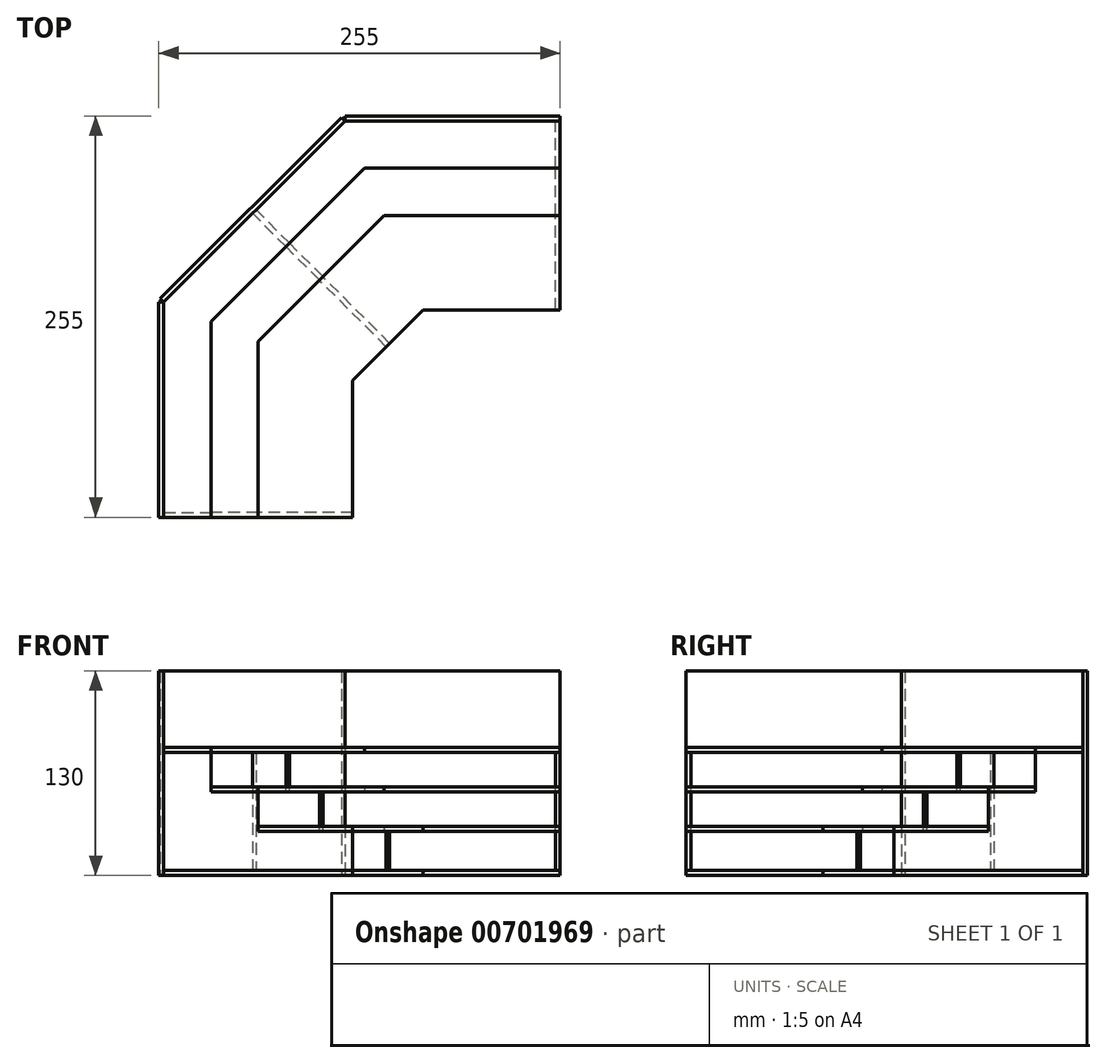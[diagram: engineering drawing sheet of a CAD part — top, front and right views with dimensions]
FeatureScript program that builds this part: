
annotation { "Feature Type Name" : "Feature", "Feature Type Description" : "" }
export const myFeature = defineFeature(function(context is Context, id is Id, definition is map)
    precondition{}
    {
        {
            assignVariable(context, id + "F0", {"name" : "x", "anyValue" : 3.15});
        }
        {
            var Q0;
            Q0=qCreatedBy(makeId("Top.planeOp"),FACE);
            var sketch = newSketch(context, id + "F1", { "sketchPlane" : qUnion([Q0])});
            skLineSegment(sketch, "E0", {"start": v(0, 0) * mm, "end": v(120, 0) * mm});
            skLineSegment(sketch, "E1", {"start": v(120, 0) * mm, "end": v(120, 87) * mm});
            skLineSegment(sketch, "E2", {"start": v(120, 87) * mm, "end": v(164.85, 131.85) * mm});
            skLineSegment(sketch, "E3", {"start": v(164.85, 131.85) * mm, "end": v(251.85, 131.85) * mm});
            skLineSegment(sketch, "E4", {"start": v(251.85, 131.85) * mm, "end": v(251.85, 251.85) * mm});
            skLineSegment(sketch, "E5", {"start": v(251.85, 251.85) * mm, "end": v(115.14, 251.85) * mm});
            skLineSegment(sketch, "E6", {"start": v(115.14, 251.85) * mm, "end": v(0, 136.7) * mm});
            skLineSegment(sketch, "E7", {"start": v(0, 136.7) * mm, "end": v(0, 0) * mm});
            skLineSegment(sketch, "E8", {"start": v(0, 136.7) * mm, "end": v(0, 251.85) * mm, "construction": true});
            skLineSegment(sketch, "E9", {"start": v(0, 251.85) * mm, "end": v(115.14, 251.85) * mm, "construction": true});
            skLineSegment(sketch, "E10", {"start": v(251.85, 131.85) * mm, "end": v(251.85, 0) * mm, "construction": true});
            skLineSegment(sketch, "E11", {"start": v(251.85, 0) * mm, "end": v(120, 0) * mm, "construction": true});
            skLineSegment(sketch, "E12", {"start": v(251.85, 0) * mm, "end": v(142.42, 109.42) * mm, "construction": true});
            skLineSegment(sketch, "E13", {"start": v(142.43, 109.42) * mm, "end": v(57.57, 194.28) * mm, "construction": true});
            skLineSegment(sketch, "E14", {"start": v(57.57, 194.28) * mm, "end": v(0, 251.85) * mm, "construction": true});
            skLineSegment(sketch, "E15.0", {"start": v(-3.15, 104.14) * mm, "end": v(-3.15, 0) * mm});
            skSolve(sketch);
        }
        {
            var Q0;
            Q0=qSketchRegion(id+"F1",true);
            extrude(context, id + "F2", {"entities" : qUnion([Q0]), "depth" : (getVariable(context, 'x')) * mm, "offsetDistance" : 25 * mm});
        }
        {
            var Q0;
            Q0=makeQuery(id+"F2.opExtrude","SWEPT_FACE",FACE,{"disambiguationData":[OSD([sQuery(id+"F1.wireOp",EDGE,"E0")])]});
            var sketch = newSketch(context, id + "F3", { "sketchPlane" : qUnion([Q0])});
            skLineSegment(sketch, "E16.bottom", {"start": v(0, 3.15) * mm, "end": v(120, 3.15) * mm});
            skLineSegment(sketch, "E16.top", {"start": v(0, 78.15) * mm, "end": v(30, 78.15) * mm});
            skLineSegment(sketch, "E16.left", {"start": v(0, 3.15) * mm, "end": v(0, 78.15) * mm});
            skLineSegment(sketch, "E16.right", {"start": v(120, 3.15) * mm, "end": v(120, 28.15) * mm});
            skLineSegment(sketch, "E17", {"start": v(120, 28.15) * mm, "end": v(60, 28.15) * mm});
            skLineSegment(sketch, "E18", {"start": v(60, 28.15) * mm, "end": v(60, 53.15) * mm});
            skLineSegment(sketch, "E19", {"start": v(60, 53.15) * mm, "end": v(30, 53.15) * mm});
            skLineSegment(sketch, "E20", {"start": v(30, 53.15) * mm, "end": v(30, 78.15) * mm});
            skSolve(sketch);
        }
        {
            var Q0;
            Q0=qSketchRegion(id+"F3",true);
            extrude(context, id + "F4", {"entities" : qUnion([Q0]), "oppositeDirection" : true, "depth" : (getVariable(context, 'x')) * mm, "offsetDistance" : 25 * mm});
        }
        {
            var Q0;
            Q0=makeQuery(id+"F2.opExtrude","SWEPT_FACE",FACE,{"disambiguationData":[OSD([sQuery(id+"F1.wireOp",EDGE,"E4")])]});
            var sketch = newSketch(context, id + "F5", { "sketchPlane" : qUnion([Q0])});
            skLineSegment(sketch, "E21.bottom", {"start": v(221.85, 78.15) * mm, "end": v(251.85, 78.15) * mm});
            skLineSegment(sketch, "E21.top", {"start": v(131.85, 3.15) * mm, "end": v(251.85, 3.15) * mm});
            skLineSegment(sketch, "E21.left", {"start": v(131.85, 28.15) * mm, "end": v(131.85, 3.15) * mm});
            skLineSegment(sketch, "E21.right", {"start": v(251.85, 78.15) * mm, "end": v(251.85, 3.15) * mm});
            skLineSegment(sketch, "E22", {"start": v(131.85, 28.15) * mm, "end": v(191.85, 28.15) * mm});
            skLineSegment(sketch, "E23", {"start": v(191.85, 28.15) * mm, "end": v(191.85, 53.15) * mm});
            skLineSegment(sketch, "E24", {"start": v(191.85, 53.15) * mm, "end": v(221.85, 53.15) * mm});
            skLineSegment(sketch, "E25", {"start": v(221.85, 53.15) * mm, "end": v(221.85, 78.15) * mm});
            skSolve(sketch);
        }
        {
            var Q0;
            Q0=qSketchRegion(id+"F5",true);
            extrude(context, id + "F6", {"entities" : qUnion([Q0]), "oppositeDirection" : true, "depth" : (getVariable(context, 'x')) * mm, "offsetDistance" : 25 * mm});
        }
        {
            var Q0;
            Q0=makeQuery(id+"F2.opExtrude","SWEPT_FACE",FACE,{"disambiguationData":[OSD([sQuery(id+"F1.wireOp",EDGE,"E7")])]});
            var sketch = newSketch(context, id + "F7", { "sketchPlane" : qUnion([Q0])});
            skLineSegment(sketch, "E26.bottom", {"start": v(0, 0) * mm, "end": v(-136.7, 0) * mm});
            skLineSegment(sketch, "E26.top", {"start": v(0, 130) * mm, "end": v(-136.7, 130) * mm});
            skLineSegment(sketch, "E26.left", {"start": v(0, 130) * mm, "end": v(0, 0) * mm});
            skLineSegment(sketch, "E26.right", {"start": v(-136.7, 130) * mm, "end": v(-136.7, 0) * mm});
            skSolve(sketch);
        }
        {
            var Q0;
            Q0=qSketchRegion(id+"F7",true);
            extrude(context, id + "F8", {"entities" : qUnion([Q0]), "depth" : (getVariable(context, 'x')) * mm, "offsetDistance" : 25 * mm});
        }
        {
            var Q0;
            Q0=makeQuery(id+"F2.opExtrude","SWEPT_FACE",FACE,{"disambiguationData":[OSD([sQuery(id+"F1.wireOp",EDGE,"E5")])]});
            var sketch = newSketch(context, id + "F9", { "sketchPlane" : qUnion([Q0])});
            skLineSegment(sketch, "E27.bottom", {"start": v(-251.85, 0) * mm, "end": v(-115.14, 0) * mm});
            skLineSegment(sketch, "E27.top", {"start": v(-251.85, 130) * mm, "end": v(-115.14, 130) * mm});
            skLineSegment(sketch, "E27.left", {"start": v(-251.85, 130) * mm, "end": v(-251.85, 0) * mm});
            skLineSegment(sketch, "E27.right", {"start": v(-115.14, 130) * mm, "end": v(-115.14, 0) * mm});
            skSolve(sketch);
        }
        {
            var Q0;
            Q0=qSketchRegion(id+"F9",true);
            extrude(context, id + "F10", {"entities" : qUnion([Q0]), "depth" : (getVariable(context, 'x')) * mm, "offsetDistance" : 25 * mm});
        }
        {
            var Q0;
            Q0=makeQuery(id+"F2.opExtrude","SWEPT_FACE",FACE,{"disambiguationData":[OSD([sQuery(id+"F1.wireOp",EDGE,"E6")])]});
            var sketch = newSketch(context, id + "F11", { "sketchPlane" : qUnion([Q0])});
            skLineSegment(sketch, "E28.bottom", {"start": v(-259.5, 0) * mm, "end": v(-96.67, 0) * mm});
            skLineSegment(sketch, "E28.top", {"start": v(-259.5, 130) * mm, "end": v(-96.67, 130) * mm});
            skLineSegment(sketch, "E28.left", {"start": v(-259.5, 130) * mm, "end": v(-259.5, 0) * mm});
            skLineSegment(sketch, "E28.right", {"start": v(-96.67, 130) * mm, "end": v(-96.67, 0) * mm});
            skSolve(sketch);
        }
        {
            var Q0;
            Q0=qSketchRegion(id+"F11",true);
            extrude(context, id + "F12", {"entities" : qUnion([Q0]), "depth" : (getVariable(context, 'x')) * mm, "offsetDistance" : 25 * mm});
        }
        {
            var Q0;
            Q0=makeQuery(id+"F12.opExtrude","CAP_EDGE",EDGE,{"disambiguationData":[OSD([sQuery(id+"F11.wireOp",EDGE,"E28.top")])],"isStart":true});
            cPoint(context, id + "F13", {"entities" : qUnion([Q0]), "parameter" : 0.5});
        }
        {
            var Q0;
            Q0=makeQuery(id+"F12.opExtrude","SWEPT_FACE",FACE,{"disambiguationData":[OSD([sQuery(id+"F11.wireOp",EDGE,"E28.right")])]});
            var Q1;
            Q1 = qCreatedBy(id + "F13" ,VERTEX);
            cPlane(context, id + "F14", {"entities" : qUnion([Q0, Q1]), "cplaneType" : CPlaneType.PLANE_POINT, "offset" : 25 * mm, "width" : 150 * mm, "height" : 150 * mm});
        }
        {
            var Q0;
            Q0=qCreatedBy(id+"F14.planeOp",FACE);
            var sketch = newSketch(context, id + "F15", { "sketchPlane" : qUnion([Q0])});
            skLineSegment(sketch, "E29", {"start": v(-96.67, 78.15) * mm, "end": v(-96.67, 3.15) * mm});
            skLineSegment(sketch, "E30", {"start": v(-96.67, 3.15) * mm, "end": v(23.33, 3.15) * mm});
            skLineSegment(sketch, "E31", {"start": v(23.33, 3.15) * mm, "end": v(23.33, 28.15) * mm});
            skLineSegment(sketch, "E32", {"start": v(23.33, 28.15) * mm, "end": v(-36.67, 28.15) * mm});
            skLineSegment(sketch, "E33", {"start": v(-36.67, 28.15) * mm, "end": v(-36.67, 53.15) * mm});
            skLineSegment(sketch, "E34", {"start": v(-36.67, 53.15) * mm, "end": v(-66.67, 53.15) * mm});
            skLineSegment(sketch, "E35", {"start": v(-66.67, 53.15) * mm, "end": v(-66.67, 78.15) * mm});
            skLineSegment(sketch, "E36", {"start": v(-66.67, 78.15) * mm, "end": v(-96.67, 78.15) * mm});
            skPoint(sketch, "E37", {"position": v(-36.67, 3.15) * mm});
            skSolve(sketch);
        }
        {
            var Q0;
            Q0 = qSketchRegion(id + "F15", true);
            extrude(context, id + "F16", {"entities" : qUnion([Q0]), "depth" : (getVariable(context, 'x') / 2) * mm, "offsetDistance" : 25 * mm, "hasSecondDirection" : true, "secondDirectionOppositeDirection" : true, "secondDirectionDepth" : (getVariable(context, 'x') / 2) * mm});
        }
        {
            var Q0;
            Q0=makeQuery(id+"F4.opExtrude","SWEPT_FACE",FACE,{"disambiguationData":[OSD([sQuery(id+"F3.wireOp",EDGE,"E17")])]});
            var sketch = newSketch(context, id + "F17", { "sketchPlane" : qUnion([Q0])});
            skLineSegment(sketch, "E38.0", {"start": v(140, 191.85) * mm, "end": v(251.85, 191.85) * mm});
            skLineSegment(sketch, "E38.1", {"start": v(60, 111.85) * mm, "end": v(140, 191.85) * mm});
            skLineSegment(sketch, "E38.2", {"start": v(60, 0) * mm, "end": v(60, 111.85) * mm});
            skLineSegment(sketch, "E39", {"start": v(60, 0) * mm, "end": v(120, 0) * mm});
            skLineSegment(sketch, "E40", {"start": v(120, 0) * mm, "end": v(120, 87) * mm});
            skLineSegment(sketch, "E41", {"start": v(120, 87) * mm, "end": v(164.85, 131.85) * mm});
            skLineSegment(sketch, "E42", {"start": v(164.85, 131.85) * mm, "end": v(251.85, 131.85) * mm});
            skLineSegment(sketch, "E43", {"start": v(251.85, 131.85) * mm, "end": v(251.85, 191.85) * mm});
            skSolve(sketch);
        }
        {
            var Q0;
            Q0 = qSketchRegion(id + "F17", true);
            extrude(context, id + "F18", {"entities" : qUnion([Q0]), "depth" : (getVariable(context, 'x')) * mm, "offsetDistance" : 25 * mm});
        }
        {
            var Q0;
            Q0=makeQuery(id+"F4.opExtrude","SWEPT_FACE",FACE,{"disambiguationData":[OSD([sQuery(id+"F3.wireOp",EDGE,"E19")])]});
            var sketch = newSketch(context, id + "F19", { "sketchPlane" : qUnion([Q0])});
            skLineSegment(sketch, "E44.0", {"start": v(127.57, 221.85) * mm, "end": v(251.85, 221.85) * mm});
            skLineSegment(sketch, "E44.1", {"start": v(30, 124.28) * mm, "end": v(127.57, 221.85) * mm});
            skLineSegment(sketch, "E44.2", {"start": v(30, 0) * mm, "end": v(30, 124.28) * mm});
            skLineSegment(sketch, "E45", {"start": v(30, 0) * mm, "end": v(60, 0) * mm});
            skLineSegment(sketch, "E46", {"start": v(60, 0) * mm, "end": v(60, 111.85) * mm});
            skLineSegment(sketch, "E47", {"start": v(60, 111.85) * mm, "end": v(140, 191.85) * mm});
            skLineSegment(sketch, "E48", {"start": v(140, 191.85) * mm, "end": v(251.85, 191.85) * mm});
            skLineSegment(sketch, "E49", {"start": v(251.85, 191.85) * mm, "end": v(251.85, 221.85) * mm});
            skSolve(sketch);
        }
        {
            var Q0;
            Q0 = qSketchRegion(id + "F19", true);
            extrude(context, id + "F20", {"entities" : qUnion([Q0]), "depth" : (getVariable(context, 'x')) * mm, "offsetDistance" : 25 * mm});
        }
        {
            var Q0;
            Q0=makeQuery(id+"F4.opExtrude","SWEPT_FACE",FACE,{"disambiguationData":[OSD([sQuery(id+"F3.wireOp",EDGE,"E16.top")])]});
            var sketch = newSketch(context, id + "F21", { "sketchPlane" : qUnion([Q0])});
            skLineSegment(sketch, "E50.0", {"start": v(0, 0) * mm, "end": v(30, 0) * mm});
            skLineSegment(sketch, "E50.1", {"start": v(30, 0) * mm, "end": v(30, 124.28) * mm});
            skLineSegment(sketch, "E50.2", {"start": v(0, 0) * mm, "end": v(0, 136.7) * mm});
            skLineSegment(sketch, "E50.3", {"start": v(30, 124.28) * mm, "end": v(127.57, 221.85) * mm});
            skLineSegment(sketch, "E50.4", {"start": v(115.14, 251.85) * mm, "end": v(0, 136.7) * mm});
            skLineSegment(sketch, "E50.5", {"start": v(251.85, 251.85) * mm, "end": v(115.14, 251.85) * mm});
            skLineSegment(sketch, "E50.6", {"start": v(251.85, 221.85) * mm, "end": v(251.85, 251.85) * mm});
            skLineSegment(sketch, "E50.7", {"start": v(127.57, 221.85) * mm, "end": v(251.85, 221.85) * mm});
            skSolve(sketch);
        }
        {
            var Q0;
            Q0 = qSketchRegion(id + "F21", true);
            extrude(context, id + "F22", {"entities" : qUnion([Q0]), "depth" : (getVariable(context, 'x')) * mm, "offsetDistance" : 25 * mm});
        }
    });
